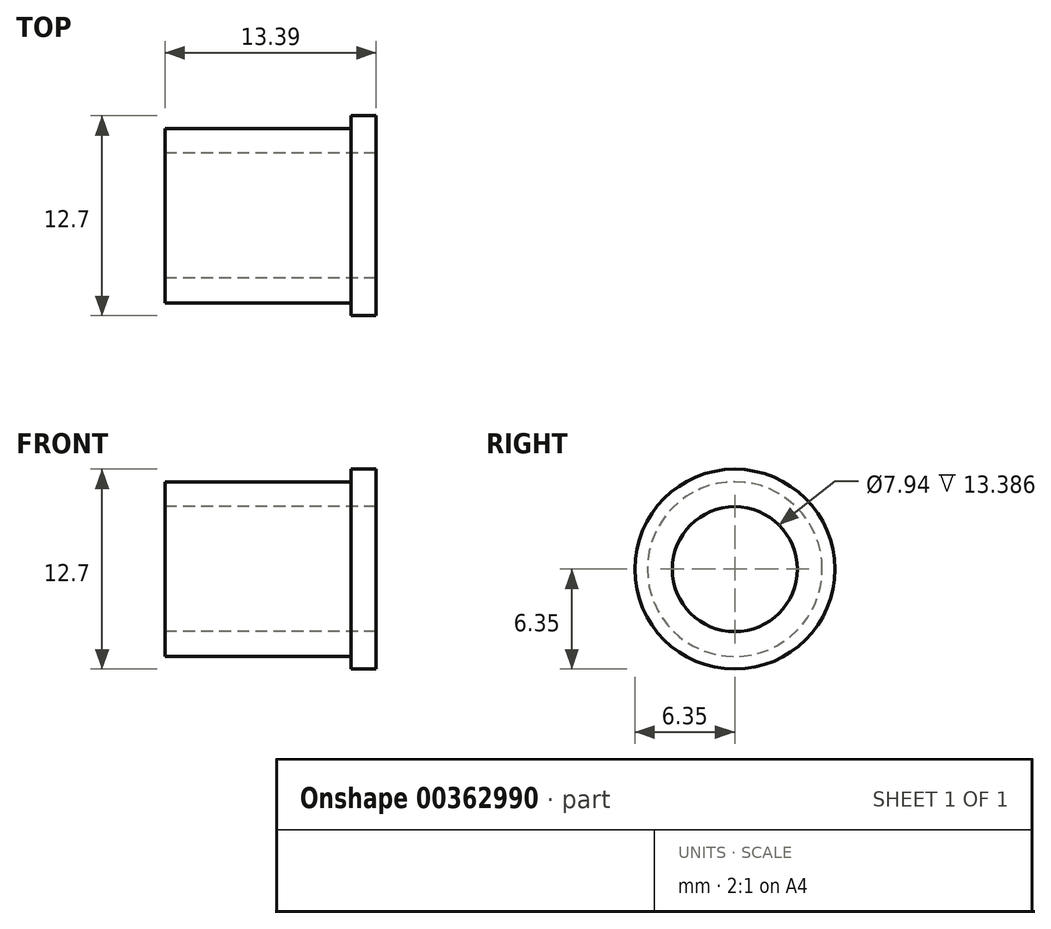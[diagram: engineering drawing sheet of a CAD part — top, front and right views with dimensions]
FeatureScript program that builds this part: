
annotation { "Feature Type Name" : "Feature", "Feature Type Description" : "" }
export const myFeature = defineFeature(function(context is Context, id is Id, definition is map)
    precondition{}
    {
        {
            var Q0;
            Q0=qCreatedBy(makeId("Front.planeOp"),FACE);
            var sketch = newSketch(context, id + "F0", { "sketchPlane" : qUnion([Q0])});
            skLineSegment(sketch, "E0", {"start": v(-33.76, 0) * mm, "end": v(-9.34, 0) * mm});
            skLineSegment(sketch, "E1", {"start": v(-30.44, 3.97) * mm, "end": v(-17.05, 3.97) * mm});
            skLineSegment(sketch, "E2", {"start": v(-17.05, 3.97) * mm, "end": v(-17.05, 6.35) * mm});
            skLineSegment(sketch, "E3", {"start": v(-17.05, 6.35) * mm, "end": v(-18.63, 6.35) * mm});
            skLineSegment(sketch, "E4", {"start": v(-18.63, 6.35) * mm, "end": v(-18.63, 5.55) * mm});
            skLineSegment(sketch, "E5", {"start": v(-18.63, 5.55) * mm, "end": v(-30.44, 5.55) * mm});
            skLineSegment(sketch, "E6", {"start": v(-30.44, 5.55) * mm, "end": v(-30.44, 3.97) * mm});
            skSolve(sketch);
        }
        {
            var Q0;
            Q0=makeQuery(id+"F0.imprint","IMPRINT",FACE,{"disambiguationData":[TD([[makeQuery(id+"F0.imprint","IMPRINT",EDGE,{"derivedFrom":sQuery(id+"F0.wireOp",EDGE,"E1")}),1.0]])]});
            var Q1;
            Q1=sQuery(id+"F0.wireOp",EDGE,"E0");
            revolve(context, id + "F1", {"entities" : qUnion([Q0]), "axis" : qUnion([Q1]), "revolveType" : RevolveType.FULL});
        }
    });
